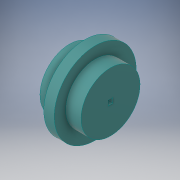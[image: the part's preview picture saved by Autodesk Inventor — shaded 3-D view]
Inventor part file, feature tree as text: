
AUTODESK INVENTOR PART (.ipt)
format: ipt  version: 2019 (Build 230136000, 136)  size: 136,704 bytes
history: native  units: in
note: dims shown in document units (in); Inventor stores cm internally (conversion verified against a paired STEP export)
features: extrude x3, sketch x3
ambient origin geometry x8: Origin, YZ Plane, XZ Plane, XY Plane, X Axis, Y Axis, Z Axis, Center Point
bodies: Solid1 (feature_tree)
feature tree (6):
  extrude  "Extrusion1"  Depth=0.9843in TaperAngle=0.0deg
  extrude  "Extrusion2"  Depth=0.25in TaperAngle=0.0deg
  extrude  "Extrusion3"  Depth=0.1181in
  sketch  "Sketch1"  dims[d0=1.4173in d1=0.9843in d2=0.0in]
  sketch  "Sketch2"  dims[d3=1.9685in d4=0.25in d5=0.0in]
  sketch  "Sketch3"  dims[d6=0.1181in d7=0.1181in d8=1.0in d9=0.0in]
